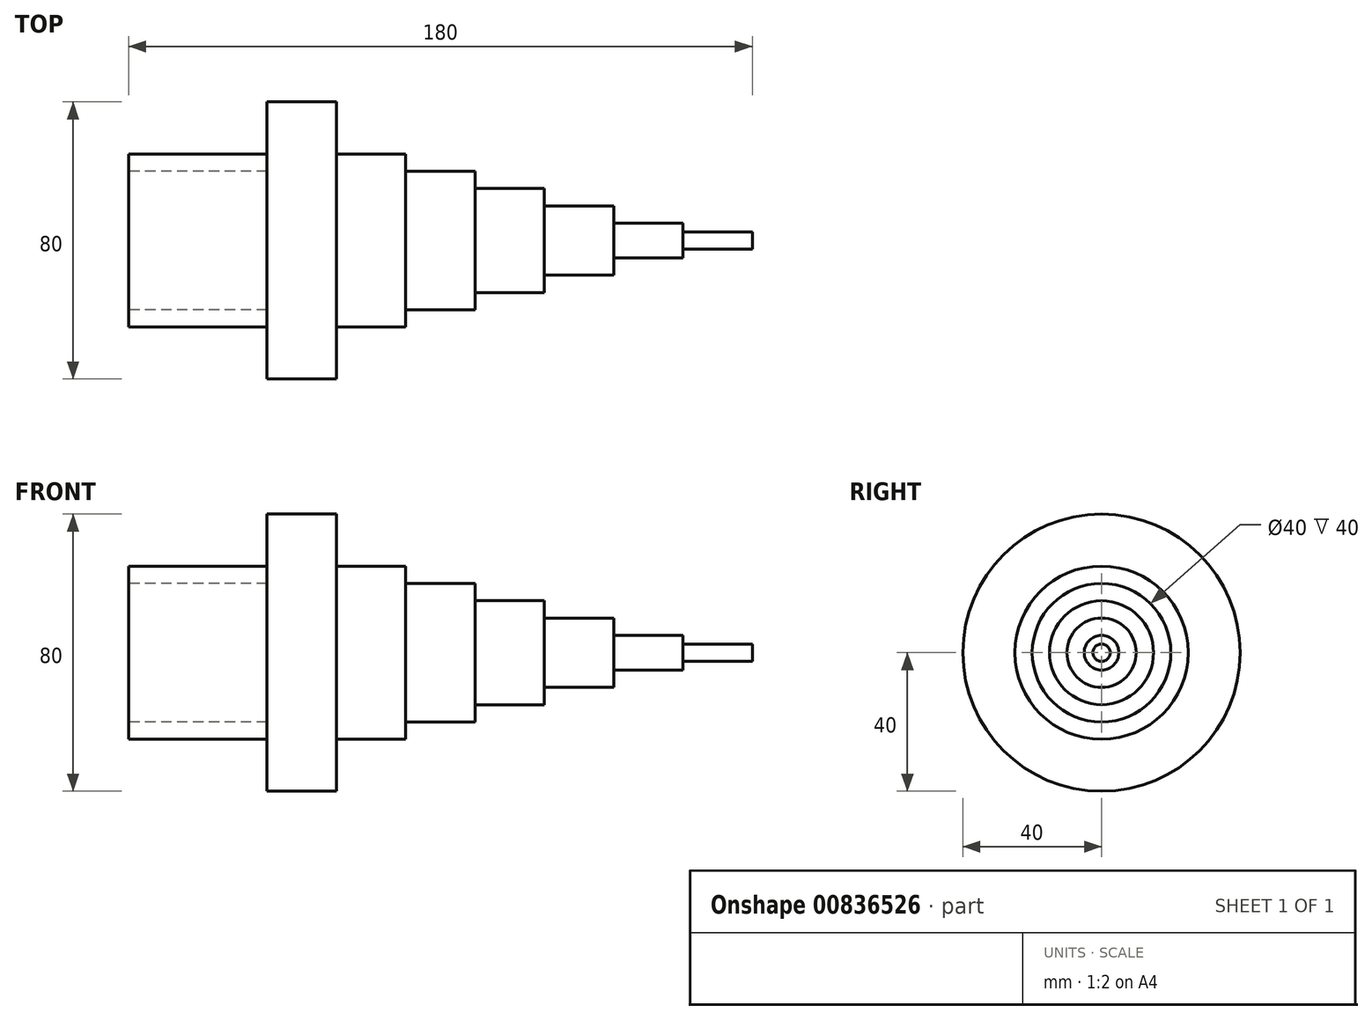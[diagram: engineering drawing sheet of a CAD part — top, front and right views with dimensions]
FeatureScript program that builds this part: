
annotation { "Feature Type Name" : "Feature", "Feature Type Description" : "" }
export const myFeature = defineFeature(function(context is Context, id is Id, definition is map)
    precondition{}
    {
        {
            var Q0;
            Q0=qCreatedBy(makeId("Front.planeOp"),FACE);
            var sketch = newSketch(context, id + "F0", { "sketchPlane" : qUnion([Q0])});
            skLineSegment(sketch, "E0", {"start": v(-90, 25) * mm, "end": v(-50, 25) * mm});
            skLineSegment(sketch, "E1", {"start": v(-30, 25) * mm, "end": v(-10, 25) * mm});
            skLineSegment(sketch, "E2", {"start": v(-10, 25) * mm, "end": v(-10, 20) * mm});
            skLineSegment(sketch, "E3", {"start": v(-10, 20) * mm, "end": v(10, 20) * mm});
            skLineSegment(sketch, "E4", {"start": v(10, 20) * mm, "end": v(10, 15) * mm});
            skLineSegment(sketch, "E5", {"start": v(10, 15) * mm, "end": v(30, 15) * mm});
            skLineSegment(sketch, "E6", {"start": v(30, 15) * mm, "end": v(30, 10) * mm});
            skLineSegment(sketch, "E7", {"start": v(30, 10) * mm, "end": v(50, 10) * mm});
            skLineSegment(sketch, "E8", {"start": v(50, 10) * mm, "end": v(50, 5) * mm});
            skLineSegment(sketch, "E9", {"start": v(50, 5) * mm, "end": v(70, 5) * mm});
            skLineSegment(sketch, "E10", {"start": v(70, 5) * mm, "end": v(70, 2.5) * mm});
            skLineSegment(sketch, "E11", {"start": v(70, 2.5) * mm, "end": v(90, 2.5) * mm});
            skLineSegment(sketch, "E12", {"start": v(90, 2.5) * mm, "end": v(90, 0) * mm});
            skLineSegment(sketch, "E13", {"start": v(-30, 25) * mm, "end": v(-30, 40) * mm});
            skLineSegment(sketch, "E14", {"start": v(-30, 40) * mm, "end": v(-50, 40) * mm});
            skLineSegment(sketch, "E15", {"start": v(-50, 40) * mm, "end": v(-50, 25) * mm});
            skLineSegment(sketch, "E16", {"start": v(-90, 25) * mm, "end": v(-90, 20) * mm});
            skLineSegment(sketch, "E17", {"start": v(-90.97, 0) * mm, "end": v(90, 0) * mm});
            skLineSegment(sketch, "E18", {"start": v(-90, 20) * mm, "end": v(-50, 20) * mm});
            skLineSegment(sketch, "E19", {"start": v(-50, 20) * mm, "end": v(-50, 0) * mm});
            skSolve(sketch);
        }
        {
            var Q0;
            Q0=makeQuery(id+"F0.imprint","IMPRINT",FACE,{"disambiguationData":[TD([[makeQuery(id+"F0.imprint","IMPRINT",EDGE,{"derivedFrom":sQuery(id+"F0.wireOp",EDGE,"E0")}),-1.0]])]});
            var Q1;
            Q1=sQuery(id+"F0.wireOp",EDGE,"E17");
            revolve(context, id + "F1", {"surfaceOperationType" : NewSurfaceOperationType.NEW, "entities" : qUnion([Q0]), "axis" : qUnion([Q1]), "revolveType" : RevolveType.FULL});
        }
    });
